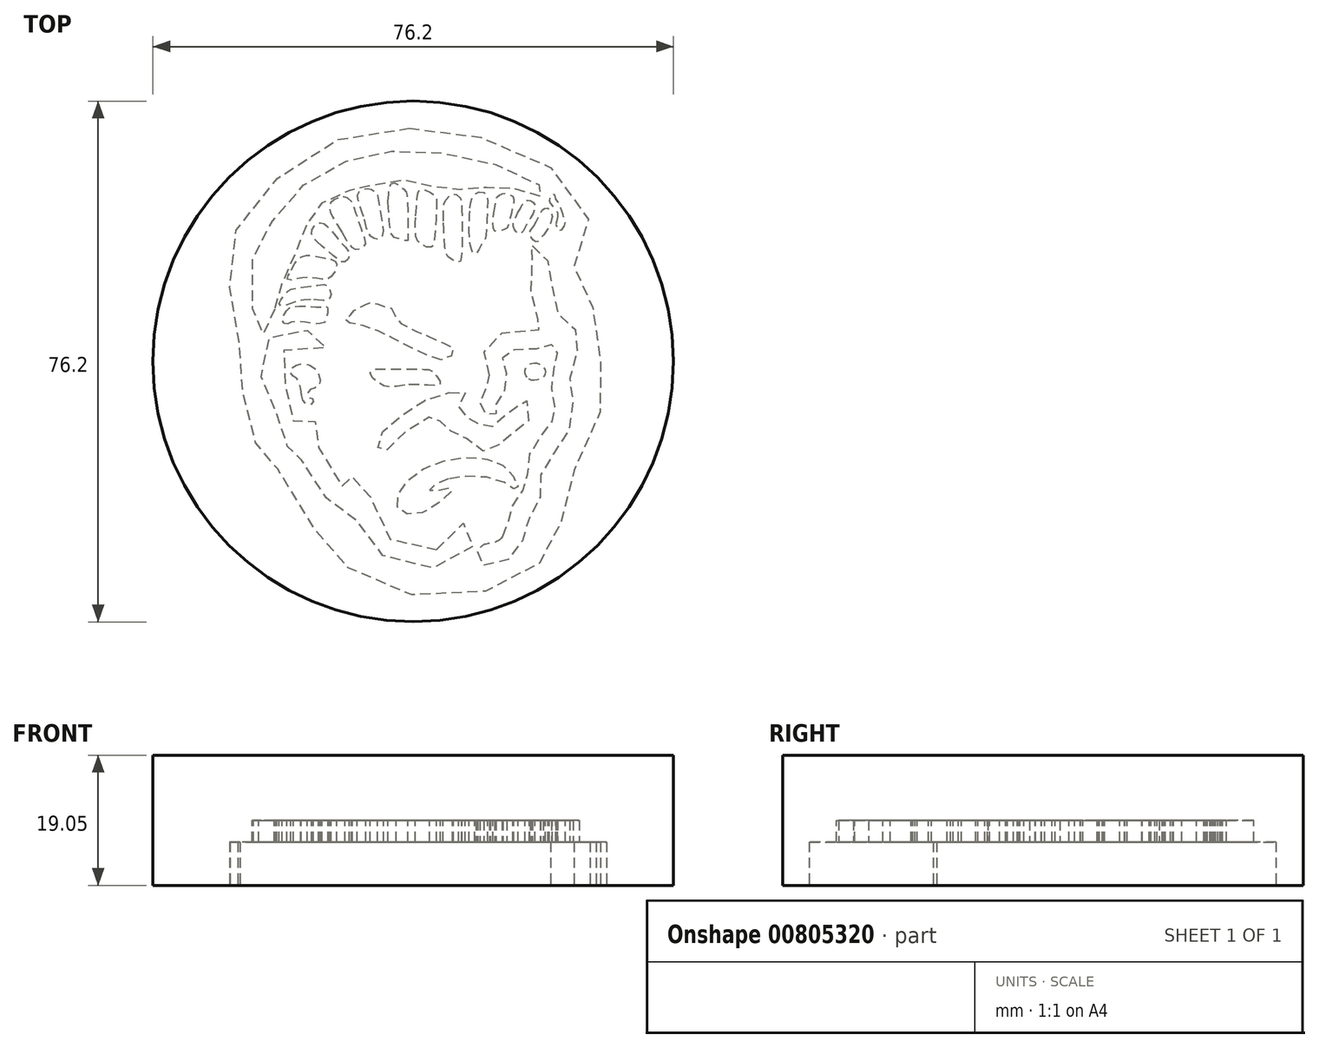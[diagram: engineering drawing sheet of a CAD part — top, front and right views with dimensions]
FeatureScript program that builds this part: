
annotation { "Feature Type Name" : "Feature", "Feature Type Description" : "" }
export const myFeature = defineFeature(function(context is Context, id is Id, definition is map)
    precondition{}
    {
        {
            var Q0;
            Q0=qCreatedBy(makeId("Top.planeOp"),FACE);
            var sketch = newSketch(context, id + "F0", { "sketchPlane" : qUnion([Q0])});
            skCircle(sketch, "E0", {"center": v(-21.46, 11.84) * mm, "radius": 38.1 * mm});
            skFitSpline(sketch, "E1", {"points": [v(-22.7, 8.38) * mm, v(-24.46, 8.12) * mm, v(-25.73, 8.25) * mm, v(-27.12, 9.13) * mm, v(-27.73, 10) * mm, v(-27.64, 10.46) * mm, v(-27.02, 10.74) * mm, v(-25.88, 10.74) * mm, v(-21.93, 10.72) * mm, v(-19.6, 10.7) * mm, v(-19.07, 10.65) * mm, v(-18.56, 10.3) * mm, v(-17.72, 9.25) * mm, v(-17.47, 8.65) * mm, v(-17.68, 8.4) * mm, v(-18.8, 8.34) * mm, v(-21.13, 8.46) * mm, v(-22.7, 8.38) * mm]});
            skFitSpline(sketch, "E2", {"points": [v(-19.46, 15.62) * mm, v(-16.33, 14.26) * mm, v(-15.7, 13.95) * mm, v(-15.58, 13.23) * mm, v(-16.19, 12.4) * mm, v(-17.49, 12.1) * mm, v(-18.69, 12.45) * mm, v(-22.9, 14.45) * mm, v(-26.26, 16.14) * mm, v(-28.77, 17.08) * mm, v(-30.77, 17.49) * mm, v(-31.33, 17.57) * mm, v(-31.4, 17.97) * mm, v(-30.9, 18.38) * mm, v(-30.54, 18.77) * mm, v(-30.4, 19.15) * mm, v(-30.09, 19.33) * mm, v(-29.57, 19.42) * mm, v(-29.27, 19.72) * mm, v(-28.97, 19.97) * mm, v(-28.62, 20.1) * mm, v(-28.14, 20.15) * mm, v(-27.78, 20.44) * mm, v(-27.45, 20.54) * mm, v(-26.96, 20.38) * mm, v(-26.02, 19.96) * mm, v(-25.67, 19.88) * mm, v(-25.26, 19.9) * mm, v(-24.65, 19.6) * mm, v(-24.36, 19.18) * mm, v(-24.08, 18.33) * mm, v(-23.23, 17.37) * mm, v(-20.38, 16) * mm, v(-19.46, 15.62) * mm]});
            skFitSpline(sketch, "E3", {"points": [v(-8.34, -13.71) * mm, v(-9.16, -14.49) * mm, v(-10.62, -14.84) * mm, v(-11.39, -15.13) * mm, v(-12.04, -15.9) * mm], "startDerivative": vector(-2.68, -3.52) * mm, "endDerivative": vector(-2.65, -3.66) * mm});
            skFitSpline(sketch, "E4", {"points": [v(-16.2, 7.28) * mm, v(-14.6, 7.44) * mm, v(-14, 7.47) * mm, v(-13.84, 7.3) * mm, v(-14.14, 6.72) * mm, v(-14.5, 6.33) * mm, v(-14.76, 5.53) * mm, v(-14.79, 4.54) * mm, v(-14.38, 3.83) * mm, v(-13.78, 3.67) * mm, v(-13.2, 3.67) * mm, v(-12.5, 3.43) * mm, v(-12.08, 2.98) * mm, v(-11.38, 2.28) * mm, v(-10.72, 2) * mm, v(-10.17, 2.13) * mm, v(-9.54, 2.62) * mm, v(-8.94, 3.23) * mm, v(-8.52, 3.7) * mm, v(-7.8, 4) * mm, v(-6.7, 4.7) * mm, v(-6.03, 5.35) * mm, v(-5.66, 6.34) * mm, v(-5.45, 6.62) * mm, v(-5.08, 6.51) * mm, v(-4.73, 5.73) * mm, v(-4.46, 4.87) * mm, v(-4.57, 3.19) * mm, v(-5.27, 2.21) * mm, v(-6.6, 1.44) * mm, v(-7.7, 0.95) * mm, v(-8.45, 0.35) * mm, v(-9.08, -0.48) * mm, v(-9.72, -0.93) * mm, v(-10.7, -1.3) * mm, v(-11.63, -1.14) * mm, v(-12.64, -0.36) * mm, v(-13.83, 0.77) * mm, v(-14.43, 1.35) * mm, v(-15.32, 1.58) * mm, v(-16.5, 1.74) * mm, v(-17.1, 2.04) * mm, v(-17.4, 2.69) * mm, v(-17.74, 3.7) * mm, v(-17.86, 3.97) * mm, v(-18.26, 3.98) * mm, v(-19.47, 3.52) * mm, v(-21.5, 2.33) * mm, v(-23.63, 0.73) * mm, v(-25.06, -0.74) * mm, v(-25.75, -1.57) * mm, v(-26.26, -1.64) * mm, v(-26.41, -1.4) * mm, v(-26.65, -0.4) * mm, v(-26.65, 0.63) * mm, v(-26.46, 1.05) * mm, v(-25.12, 2.31) * mm, v(-23.58, 3.62) * mm, v(-21.96, 4.78) * mm, v(-19.93, 6.09) * mm, v(-17.62, 6.91) * mm, v(-16.2, 7.28) * mm]});
            skFitSpline(sketch, "E5", {"points": [v(-10.28, 9.87) * mm, v(-10.8, 11.15) * mm, v(-11.14, 12.51) * mm, v(-10.82, 14.14) * mm, v(-9.8, 15.47) * mm, v(-6.9, 16.25) * mm, v(-3.3, 16.48) * mm, v(-2.63, 16.62) * mm, v(-2.43, 16.79) * mm, v(-2.45, 17.06) * mm, v(-2.8, 17.38) * mm, v(-3.58, 18.79) * mm, v(-4.01, 20.41) * mm, v(-4.22, 23.73) * mm, v(-4.07, 26.05) * mm, v(-4.04, 27.3) * mm, v(-4.26, 28.27) * mm, v(-4.32, 28.66) * mm, v(-4.27, 28.82) * mm, v(-4.11, 28.83) * mm, v(-3.63, 28.66) * mm, v(-2.4, 27.71) * mm, v(-1.66, 26.12) * mm, v(-1.4, 24.83) * mm, v(-1.07, 22.35) * mm, v(-0.84, 20.59) * mm, v(-0.33, 18.92) * mm, v(0.72, 17.53) * mm, v(1.8, 16.95) * mm, v(2.6, 16.11) * mm, v(2.82, 15.4) * mm, v(2.62, 13.6) * mm, v(1.98, 11.41) * mm, v(1.5, 9.72) * mm, v(1.46, 8.37) * mm, v(1.67, 7.02) * mm, v(1.95, 5.46) * mm, v(1.83, 3.42) * mm, v(1.26, 1.69) * mm, v(0.3, 0.12) * mm, v(-0.82, -1.47) * mm, v(-2.19, -3.23) * mm, v(-2.76, -4.53) * mm, v(-2.84, -5.37) * mm, v(-2.78, -6.8) * mm, v(-2.9, -8.04) * mm, v(-3.46, -9.77) * mm, v(-4.42, -11.17) * mm, v(-5.17, -12.34) * mm, v(-5.44, -13.28) * mm, v(-5.5, -14.46) * mm, v(-5.87, -15.61) * mm, v(-7.05, -16.8) * mm, v(-8.61, -17.68) * mm, v(-10.24, -18.06) * mm, v(-11.68, -17.83) * mm, v(-12.24, -17.16) * mm, v(-12.17, -16.33) * mm, v(-12.04, -15.9) * mm], "startDerivative": vector(-31.41, 73.1) * mm, "endDerivative": vector(13.02, 38.55) * mm});
            skFitSpline(sketch, "E6", {"points": [v(-8.34, -13.71) * mm, v(-7.97, -13.17) * mm, v(-7.67, -12.28) * mm, v(-7.45, -10.91) * mm, v(-7.1, -9.74) * mm, v(-6.65, -8.82) * mm, v(-5.7, -7.52) * mm, v(-4.97, -6.2) * mm, v(-4.76, -5.22) * mm, v(-4.62, -3.43) * mm, v(-4.38, -1.8) * mm, v(-3.68, -0.4) * mm, v(-2.64, 1.06) * mm, v(-1.5, 2.47) * mm, v(-0.86, 3.57) * mm, v(-0.62, 4.41) * mm, v(-0.75, 5.56) * mm, v(-1.04, 6.7) * mm, v(-1.2, 8.55) * mm, v(-1.02, 10.18) * mm, v(-0.68, 11.24) * mm, v(-0.4, 12.3) * mm, v(-0.34, 13.63) * mm, v(-0.46, 14.24) * mm, v(-1.03, 14.32) * mm, v(-1.67, 14.21) * mm, v(-2.6, 13.8) * mm, v(-4.73, 13.63) * mm, v(-6.65, 13.56) * mm, v(-7.69, 13.29) * mm, v(-8.34, 12.55) * mm, v(-8.34, 11.43) * mm, v(-7.97, 10.54) * mm, v(-7.79, 9.5) * mm, v(-7.95, 8.16) * mm, v(-8.51, 6.76) * mm, v(-9.16, 6) * mm, v(-9.42, 5.3) * mm, v(-9.51, 4.8) * mm, v(-9.38, 4.46) * mm, v(-9.34, 4.3) * mm, v(-9.44, 3.95) * mm, v(-9.66, 3.78) * mm, v(-10.44, 3.95) * mm, v(-11.25, 4.46) * mm, v(-11.68, 5.16) * mm, v(-11.67, 5.7) * mm, v(-11.14, 7.15) * mm, v(-10.55, 8.4) * mm, v(-10.3, 8.96) * mm, v(-10.2, 9.48) * mm, v(-10.28, 9.87) * mm], "startDerivative": vector(25.13, 32.28) * mm, "endDerivative": vector(-8.83, 30.87) * mm});
            skFitSpline(sketch, "E7", {"points": [v(-16.3, -5.35) * mm, v(-17.56, -5.82) * mm, v(-18.63, -6.38) * mm, v(-19, -6.8) * mm, v(-19.06, -7.06) * mm, v(-18.95, -7.18) * mm, v(-18.44, -7.12) * mm, v(-16.9, -6.78) * mm, v(-15.96, -6.63) * mm, v(-15.75, -6.63) * mm, v(-15.68, -6.77) * mm, v(-15.87, -7.2) * mm, v(-17.23, -8.44) * mm, v(-19.42, -10.03) * mm, v(-21.48, -10.54) * mm, v(-22.84, -10.31) * mm, v(-23.65, -9.65) * mm, v(-23.95, -8.73) * mm, v(-23.49, -7.3) * mm, v(-22.29, -5.6) * mm, v(-19.82, -3.8) * mm, v(-16.58, -2.6) * mm, v(-12.68, -2.18) * mm, v(-9.83, -2.66) * mm, v(-8.1, -3.52) * mm, v(-6.95, -4.79) * mm, v(-6.37, -5.83) * mm, v(-6.14, -6.5) * mm, v(-6.28, -6.87) * mm, v(-6.45, -6.91) * mm, v(-6.72, -6.82) * mm, v(-7.28, -6.32) * mm, v(-8.44, -5.73) * mm, v(-10.94, -5.07) * mm, v(-14.3, -5.02) * mm, v(-16.3, -5.35) * mm]});
            skFitSpline(sketch, "E8", {"points": [v(-37.78, 6.92) * mm, v(-37.98, 8.08) * mm, v(-38.1, 8.82) * mm, v(-38.62, 9.46) * mm, v(-39.1, 9.74) * mm, v(-39.35, 10) * mm, v(-39.35, 10.7) * mm, v(-38.68, 11.25) * mm, v(-37.66, 11.55) * mm, v(-36.18, 11.08) * mm, v(-35.45, 10.27) * mm, v(-35.08, 9.24) * mm, v(-35.25, 8.36) * mm, v(-35.73, 8) * mm, v(-36.32, 7.83) * mm, v(-36.75, 7.55) * mm, v(-36.94, 6.93) * mm, v(-36.58, 6.41) * mm, v(-36.17, 6.4) * mm, v(-36.06, 6.25) * mm, v(-36.2, 5.74) * mm, v(-36.56, 5.5) * mm, v(-37.1, 5.58) * mm, v(-37.58, 6.1) * mm, v(-37.78, 6.92) * mm]});
            skFitSpline(sketch, "E9", {"points": [v(-0.35, 33) * mm, v(-0.52, 32.23) * mm, v(-0.58, 31.86) * mm, v(-0.34, 31.2) * mm, v(0, 30.97) * mm, v(0.3, 31.15) * mm, v(0.74, 31.87) * mm, v(0.8, 32.31) * mm, v(0.58, 32.88) * mm, v(0.37, 33.6) * mm, v(0.15, 34.22) * mm, v(0.08, 34.64) * mm, v(-0.1, 35.06) * mm, v(-0.52, 35.44) * mm, v(-0.73, 36.12) * mm, v(-0.84, 36.3) * mm, v(-1.35, 36.1) * mm, v(-1.5, 35.57) * mm, v(-1.5, 35.14) * mm, v(-1.26, 34.77) * mm, v(-0.64, 34.17) * mm, v(-0.37, 33.68) * mm, v(-0.35, 33) * mm]});
            skFitSpline(sketch, "E10", {"points": [v(-18.03, -15.7) * mm, v(-16.44, -15.2) * mm, v(-15.76, -14.53) * mm, v(-15.18, -13.05) * mm, v(-14.38, -12.02) * mm, v(-13.72, -11.64) * mm, v(-13.19, -11.75) * mm, v(-12.68, -12.16) * mm, v(-12.49, -13.04) * mm, v(-12.48, -14.23) * mm, v(-12.9, -15.59) * mm, v(-13.93, -16.9) * mm, v(-15.22, -17.8) * mm, v(-17.58, -18.33) * mm, v(-20.4, -18.32) * mm, v(-22.73, -17.93) * mm, v(-24.72, -17.19) * mm, v(-26.52, -16.15) * mm, v(-27.86, -14.93) * mm, v(-28.79, -13.4) * mm, v(-29.5, -11.97) * mm, v(-29.65, -11.48) * mm, v(-29.9, -11.26) * mm, v(-31.11, -10.42) * mm, v(-32.43, -9.65) * mm, v(-33.62, -8.69) * mm, v(-35.17, -7.19) * mm, v(-36.5, -5.72) * mm, v(-37.44, -4.06) * mm, v(-37.73, -2.8) * mm, v(-37.94, -1.84) * mm, v(-37.88, -1.01) * mm, v(-37.87, -0.32) * mm, v(-38, -0.14) * mm, v(-39.22, -0.46) * mm, v(-39.8, -0.58) * mm, v(-40.4, -0.48) * mm, v(-40.96, 0.21) * mm, v(-41.15, 1.82) * mm, v(-41.24, 3.22) * mm, v(-41.4, 4.19) * mm, v(-41.43, 5.53) * mm, v(-41.85, 6.91) * mm, v(-42.84, 8.28) * mm, v(-43.7, 9.56) * mm, v(-44.07, 11.28) * mm, v(-43.83, 12.72) * mm, v(-43.23, 14.16) * mm, v(-42.6, 15.23) * mm, v(-42.1, 15.77) * mm, v(-41.78, 15.9) * mm, v(-40.2, 16.08) * mm, v(-37.97, 16.34) * mm, v(-36.78, 16.42) * mm, v(-35.26, 16.4) * mm, v(-34.26, 16.01) * mm, v(-33.91, 15.45) * mm, v(-33.9, 14.62) * mm, v(-34.35, 13.75) * mm, v(-35.4, 13.27) * mm, v(-36.38, 13.16) * mm, v(-37.7, 13.47) * mm, v(-40.42, 13.46) * mm, v(-41.36, 12.87) * mm, v(-41.7, 11.74) * mm, v(-41.37, 10.64) * mm, v(-40.44, 8.94) * mm, v(-39.86, 7.83) * mm, v(-39.45, 6.94) * mm, v(-39.22, 5.52) * mm, v(-39.02, 4) * mm, v(-39.01, 3.04) * mm, v(-39.01, 2.43) * mm, v(-39.01, 2.3) * mm, v(-38.9, 2.28) * mm, v(-37.98, 2.3) * mm, v(-37.15, 2.34) * mm, v(-36.5, 2.67) * mm, v(-35.42, 3.22) * mm, v(-35.06, 3.3) * mm, v(-34.85, 3.19) * mm, v(-34.81, 2.87) * mm, v(-35.03, 1.82) * mm, v(-35.3, -0.2) * mm, v(-35.17, -1.62) * mm, v(-34.56, -3.1) * mm, v(-33.4, -4.75) * mm, v(-32, -6.31) * mm, v(-31.04, -7.24) * mm, v(-30.76, -7.44) * mm, v(-30.44, -7.42) * mm, v(-30.39, -7.16) * mm, v(-30.42, -6.26) * mm, v(-30.47, -5.36) * mm, v(-30.29, -4.8) * mm, v(-29.76, -4.5) * mm, v(-29.06, -4.67) * mm, v(-28.41, -5.14) * mm, v(-28.12, -5.84) * mm, v(-27.56, -8.98) * mm, v(-27.27, -10.6) * mm, v(-26.57, -12.15) * mm, v(-25.24, -13.86) * mm, v(-23.9, -14.7) * mm, v(-21.78, -15.6) * mm, v(-18.95, -15.73) * mm, v(-18.03, -15.7) * mm]});
            skFitSpline(sketch, "E11", {"points": [v(-41.76, 19.52) * mm, v(-41.8, 18.13) * mm, v(-42.27, 16.92) * mm, v(-43.02, 16.42) * mm, v(-43.35, 16.02) * mm, v(-43.41, 15.76) * mm, v(-43.53, 15.67) * mm, v(-43.96, 15.76) * mm, v(-44.4, 16.3) * mm, v(-44.85, 18.35) * mm, v(-45, 20.95) * mm, v(-44.86, 23.72) * mm, v(-44.96, 26.89) * mm, v(-44.78, 28.55) * mm, v(-44.14, 29.62) * mm, v(-42.13, 32.29) * mm, v(-40.8, 34.1) * mm, v(-39.06, 36.15) * mm, v(-36.82, 38.2) * mm, v(-34.37, 39.76) * mm, v(-31.94, 40.88) * mm, v(-29.27, 41.83) * mm, v(-27.07, 42.36) * mm, v(-24.67, 42.6) * mm, v(-22.74, 42.69) * mm, v(-19.66, 42.5) * mm, v(-15.32, 42.13) * mm, v(-11.21, 41.18) * mm, v(-9.13, 40.58) * mm, v(-6.75, 39.58) * mm, v(-4.13, 38.34) * mm, v(-2.5, 37.25) * mm, v(-1.86, 36.63) * mm, v(-1.73, 36.37) * mm, v(-1.95, 36.05) * mm, v(-2.34, 35.65) * mm, v(-2.65, 35.84) * mm, v(-3.12, 36.2) * mm, v(-3.61, 36.48) * mm, v(-4.84, 36.56) * mm, v(-5.74, 36.66) * mm, v(-6.6, 37.08) * mm, v(-7.36, 37.36) * mm, v(-8.7, 37.3) * mm, v(-9.36, 37.05) * mm, v(-10.3, 37.17) * mm, v(-11.06, 37.37) * mm, v(-11.98, 37.37) * mm, v(-12.98, 36.88) * mm, v(-13.62, 36.67) * mm, v(-14.49, 36.96) * mm, v(-15.25, 37.11) * mm, v(-16.31, 37.03) * mm, v(-17.13, 36.8) * mm, v(-18.03, 36.97) * mm, v(-18.96, 37.84) * mm, v(-20.33, 38.14) * mm, v(-21.22, 37.97) * mm, v(-21.98, 38.04) * mm, v(-23.14, 38.52) * mm, v(-24, 38.69) * mm, v(-25.3, 38.54) * mm, v(-25.96, 37.85) * mm, v(-26.72, 37.73) * mm, v(-27.87, 37.77) * mm, v(-29.25, 37.65) * mm, v(-30.12, 37.2) * mm, v(-30.55, 36.9) * mm, v(-31.55, 36.82) * mm, v(-32.56, 36.69) * mm, v(-33.55, 36.2) * mm, v(-34.7, 35.3) * mm, v(-35, 34.39) * mm, v(-35.15, 33.79) * mm, v(-35.7, 33.23) * mm, v(-36.32, 32.9) * mm, v(-37.06, 31.86) * mm, v(-37.54, 30.73) * mm, v(-37.7, 28.97) * mm, v(-37.85, 28.62) * mm, v(-38.16, 28.32) * mm, v(-39.21, 27.19) * mm, v(-40, 26.15) * mm, v(-40.5, 25.05) * mm, v(-40.69, 23.35) * mm, v(-40.76, 22.48) * mm, v(-40.96, 22.22) * mm, v(-41.35, 21.67) * mm, v(-41.72, 20.77) * mm, v(-41.76, 19.52) * mm]});
            skFitSpline(sketch, "E12", {"points": [v(-39.33, 17.58) * mm, v(-39.77, 17.37) * mm, v(-40.12, 17.37) * mm, v(-40.6, 17.63) * mm, v(-40.48, 18.46) * mm, v(-40.05, 19.21) * mm, v(-39.6, 19.66) * mm, v(-38.8, 19.83) * mm, v(-37.6, 19.94) * mm, v(-36.67, 19.88) * mm, v(-35.56, 19.8) * mm, v(-34.7, 19.88) * mm, v(-34.24, 19.96) * mm, v(-33.95, 19.6) * mm, v(-34.07, 18.54) * mm, v(-34.35, 17.65) * mm, v(-34.74, 17.45) * mm, v(-35.64, 17.3) * mm, v(-36.45, 17.45) * mm, v(-37.6, 17.63) * mm, v(-39.33, 17.58) * mm]});
            skFitSpline(sketch, "E13", {"points": [v(-36.44, 20.86) * mm, v(-37.97, 20.81) * mm, v(-39.25, 20.4) * mm, v(-40.42, 19.94) * mm, v(-40.73, 19.9) * mm, v(-41.05, 20.13) * mm, v(-41.03, 20.42) * mm, v(-40.78, 20.95) * mm, v(-40.05, 21.86) * mm, v(-39.64, 22.28) * mm, v(-39.16, 22.44) * mm, v(-37.98, 22.66) * mm, v(-36.5, 22.87) * mm, v(-35.04, 23.05) * mm, v(-34.27, 23.06) * mm, v(-33.89, 22.82) * mm, v(-33.54, 22.03) * mm, v(-33.47, 21.52) * mm, v(-33.72, 21) * mm, v(-34, 20.85) * mm, v(-34.5, 20.75) * mm, v(-35.17, 20.83) * mm, v(-36.44, 20.86) * mm]});
            skFitSpline(sketch, "E14", {"points": [v(-39.31, 25.2) * mm, v(-38.56, 26.57) * mm, v(-38.1, 27) * mm, v(-37.5, 27.3) * mm, v(-36.82, 27.39) * mm, v(-35.87, 27.25) * mm, v(-34.7, 27.01) * mm, v(-33.26, 26.7) * mm, v(-32.8, 26.42) * mm, v(-32.64, 26.1) * mm, v(-32.7, 25.73) * mm, v(-32.93, 24.95) * mm, v(-33.1, 24.69) * mm, v(-33.76, 24.02) * mm, v(-34.41, 23.8) * mm, v(-35.1, 23.93) * mm, v(-36.39, 24.11) * mm, v(-37.98, 24.06) * mm, v(-38.7, 23.86) * mm, v(-39.62, 23.79) * mm, v(-39.92, 23.92) * mm, v(-39.84, 24.22) * mm, v(-39.31, 25.2) * mm]});
            skFitSpline(sketch, "E15", {"points": [v(-34.8, 28.67) * mm, v(-36.21, 30.12) * mm, v(-36.35, 30.7) * mm, v(-36.12, 31.48) * mm, v(-35.46, 32.02) * mm, v(-35, 32.13) * mm, v(-34.35, 31.88) * mm, v(-33.58, 31.09) * mm, v(-32.7, 30.07) * mm, v(-31.63, 28.83) * mm, v(-30.87, 27.73) * mm, v(-30.86, 27.03) * mm, v(-31.4, 26.44) * mm, v(-32, 26.44) * mm, v(-32.88, 27.1) * mm, v(-34.8, 28.67) * mm]});
            skFitSpline(sketch, "E16", {"points": [v(-31.91, 30.73) * mm, v(-31, 29.15) * mm, v(-30.56, 28.65) * mm, v(-30, 28.28) * mm, v(-29.29, 28.3) * mm, v(-28.75, 28.57) * mm, v(-28.41, 29.1) * mm, v(-28.98, 31.09) * mm, v(-29.72, 33.26) * mm, v(-30.34, 35) * mm, v(-30.97, 35.68) * mm, v(-31.66, 35.91) * mm, v(-32.33, 35.77) * mm, v(-33.3, 35.34) * mm, v(-33.67, 34.7) * mm, v(-33.63, 33.9) * mm, v(-33.35, 33.2) * mm, v(-31.91, 30.73) * mm]});
            skFitSpline(sketch, "E17", {"points": [v(-28.67, 32.63) * mm, v(-28.15, 30.8) * mm, v(-27.87, 30.37) * mm, v(-27.06, 29.81) * mm, v(-26.62, 29.77) * mm, v(-26.11, 29.95) * mm, v(-25.9, 30.35) * mm, v(-25.82, 31.26) * mm, v(-26.23, 33.91) * mm, v(-26.55, 35.82) * mm, v(-26.82, 36.42) * mm, v(-27.49, 36.9) * mm, v(-28.23, 37.07) * mm, v(-29.1, 36.85) * mm, v(-29.58, 36.4) * mm, v(-29.64, 35.85) * mm, v(-29.38, 34.9) * mm, v(-28.67, 32.63) * mm]});
            skFitSpline(sketch, "E18", {"points": [v(-25.14, 35.22) * mm, v(-24.93, 37.26) * mm, v(-24.73, 37.82) * mm, v(-24.3, 37.97) * mm, v(-23.7, 37.72) * mm, v(-22.67, 36.87) * mm, v(-22.44, 36.5) * mm, v(-22.33, 36) * mm, v(-22.24, 33.1) * mm, v(-22.21, 30.55) * mm, v(-22.22, 29.61) * mm, v(-22.28, 29.46) * mm, v(-22.83, 29.57) * mm, v(-24.15, 29.97) * mm, v(-24.66, 30.54) * mm, v(-24.92, 32.1) * mm, v(-25.06, 34.07) * mm, v(-25.14, 35.22) * mm]});
            skFitSpline(sketch, "E19", {"points": [v(-21.08, 33.16) * mm, v(-20.87, 35.88) * mm, v(-20.72, 36.67) * mm, v(-20.41, 37) * mm, v(-19.98, 37.03) * mm, v(-19.36, 36.79) * mm, v(-18.35, 36.15) * mm, v(-18.07, 35.64) * mm, v(-18.02, 34.9) * mm, v(-18.18, 32.04) * mm, v(-18.51, 28.8) * mm, v(-18.63, 28.65) * mm, v(-19.18, 28.5) * mm, v(-20.17, 28.92) * mm, v(-20.9, 29.6) * mm, v(-21.14, 31.32) * mm, v(-21.08, 33.16) * mm]});
            skFitSpline(sketch, "E20", {"points": [v(-17.06, 32.41) * mm, v(-16.97, 34.72) * mm, v(-16.8, 35.25) * mm, v(-16.35, 35.9) * mm, v(-15.62, 36.3) * mm, v(-15.37, 36.34) * mm, v(-15.08, 36.24) * mm, v(-14.52, 35.71) * mm, v(-14.34, 34.83) * mm, v(-14.33, 32.77) * mm, v(-14.28, 30.12) * mm, v(-14.4, 27.24) * mm, v(-14.5, 26.6) * mm, v(-14.83, 26.3) * mm, v(-15.26, 26.47) * mm, v(-16.23, 27.01) * mm, v(-16.59, 27.44) * mm, v(-16.78, 28.15) * mm, v(-16.94, 30.31) * mm, v(-17.06, 32.41) * mm]});
            skFitSpline(sketch, "E21", {"points": [v(-13.15, 34.3) * mm, v(-13.01, 35.32) * mm, v(-12.72, 36) * mm, v(-12.1, 36.5) * mm, v(-11.6, 36.63) * mm, v(-10.83, 36.45) * mm, v(-10.6, 35.97) * mm, v(-10.62, 33.4) * mm, v(-10.74, 31.17) * mm, v(-10.9, 29.84) * mm, v(-10.98, 29.66) * mm, v(-11.55, 28.87) * mm, v(-12.2, 27.66) * mm, v(-12.36, 27.63) * mm, v(-12.73, 27.64) * mm, v(-12.82, 27.84) * mm, v(-13.09, 28.77) * mm, v(-13.26, 30.35) * mm, v(-13.25, 32.55) * mm, v(-13.15, 34.3) * mm]});
            skFitSpline(sketch, "E22", {"points": [v(-9.64, 33.51) * mm, v(-9.3, 35.68) * mm, v(-9.22, 35.89) * mm, v(-8.65, 36.3) * mm, v(-8.2, 36.42) * mm, v(-7.76, 36.4) * mm, v(-6.9, 35.99) * mm, v(-6.72, 35.56) * mm, v(-6.81, 34.83) * mm, v(-7.15, 33.37) * mm, v(-7.61, 31.53) * mm, v(-7.73, 31.37) * mm, v(-8.16, 31.1) * mm, v(-9.03, 30.84) * mm, v(-9.4, 30.86) * mm, v(-9.68, 31.08) * mm, v(-9.79, 32.51) * mm, v(-9.64, 33.51) * mm]});
            skFitSpline(sketch, "E23", {"points": [v(-6.15, 33.57) * mm, v(-5.46, 34.84) * mm, v(-5.23, 35.23) * mm, v(-4.75, 35.4) * mm, v(-4.12, 35.27) * mm, v(-3.63, 34.71) * mm, v(-3.92, 33.46) * mm, v(-5, 31.62) * mm, v(-5.64, 30.6) * mm, v(-6.2, 30.61) * mm, v(-6.7, 31.27) * mm, v(-6.85, 31.72) * mm, v(-6.72, 32.36) * mm, v(-6.15, 33.57) * mm]});
            skFitSpline(sketch, "E24", {"points": [v(-3.85, 31.62) * mm, v(-2.92, 33.33) * mm, v(-2.59, 33.99) * mm, v(-2.31, 34.21) * mm, v(-1.74, 34.26) * mm, v(-1.43, 34) * mm, v(-1.1, 33.14) * mm, v(-1.2, 32.62) * mm, v(-1.54, 31.63) * mm, v(-2.26, 30.5) * mm, v(-3.1, 29.48) * mm, v(-3.42, 29.3) * mm, v(-3.8, 29.5) * mm, v(-4.34, 30.22) * mm, v(-4.46, 30.56) * mm, v(-4.33, 30.87) * mm, v(-3.85, 31.62) * mm]});
            skFitSpline(sketch, "E25", {"points": [v(-4.77, 9.5) * mm, v(-5.07, 10.15) * mm, v(-4.95, 10.97) * mm, v(-4.45, 11.45) * mm, v(-3.72, 11.63) * mm, v(-2.73, 11.33) * mm, v(-2.25, 10.78) * mm, v(-2.1, 10.18) * mm, v(-2.46, 9.5) * mm, v(-3.2, 9.15) * mm, v(-4.13, 9.1) * mm, v(-4.77, 9.5) * mm]});
            skFitSpline(sketch, "E26", {"points": [v(-22.05, 45.95) * mm, v(-17.92, 45.68) * mm, v(-11.6, 44.65) * mm, v(-5.61, 42.66) * mm, v(-0.67, 39.74) * mm, v(3.08, 35.89) * mm, v(4.17, 32.77) * mm, v(4.3, 30.75) * mm, v(2.35, 27.01) * mm, v(2.08, 25.88) * mm, v(2.6, 22.98) * mm, v(3.24, 20.67) * mm, v(4.62, 19.86) * mm, v(6.24, 18.53) * mm, v(6.8, 15.12) * mm, v(5.46, 9.9) * mm, v(5.43, 7.3) * mm, v(5.73, 5.27) * mm, v(5.83, 2.93) * mm, v(3.06, -2.52) * mm, v(1.93, -4.48) * mm, v(1.7, -6.5) * mm, v(1.22, -9.78) * mm, v(-1.03, -13.64) * mm, v(-1.33, -14.77) * mm, v(-1.45, -15.8) * mm, v(-3.92, -18.48) * mm, v(-6.88, -20.35) * mm, v(-10.55, -21.71) * mm, v(-14.6, -22.17) * mm, v(-21.46, -22.33) * mm, v(-26.7, -21.2) * mm, v(-30.8, -18.56) * mm, v(-32.67, -15.5) * mm, v(-33.62, -14.15) * mm, v(-36.3, -12.46) * mm, v(-40.46, -7.66) * mm, v(-41.37, -3.76) * mm, v(-41.64, -3.78) * mm, v(-42.88, -4.22) * mm, v(-43.82, -3.24) * mm, v(-44.64, 1.28) * mm, v(-44.86, 4.54) * mm, v(-45.84, 6.58) * mm, v(-47, 8.65) * mm, v(-47, 11.84) * mm, v(-46.88, 14.32) * mm, v(-47.44, 16.22) * mm, v(-48.28, 19.88) * mm, v(-48.3, 23.58) * mm, v(-48.28, 28.76) * mm, v(-48.22, 29) * mm, v(-47.18, 31.44) * mm, v(-44.86, 34.56) * mm, v(-41.6, 38.38) * mm, v(-37.42, 41.78) * mm, v(-32.72, 44.22) * mm, v(-28.04, 45.58) * mm, v(-22.05, 45.95) * mm]});
            skSolve(sketch);
        }
        {
            var Q0;
            Q0=makeQuery(id+"F0.imprint","IMPRINT",FACE,{"disambiguationData":[TD([[makeQuery(id+"F0.imprint","IMPRINT",EDGE,{"derivedFrom":sQuery(id+"F0.wireOp",EDGE,"E0")}),1.0]])]});
            var Q1;
            Q1=makeQuery(id+"F0.imprint","IMPRINT",FACE,{"disambiguationData":[TD([[makeQuery(id+"F0.imprint","IMPRINT",EDGE,{"derivedFrom":sQuery(id+"F0.wireOp",EDGE,"E1")}),1.0]])]});
            var Q2;
            Q2=makeQuery(id+"F0.imprint","IMPRINT",FACE,{"disambiguationData":[TD([[makeQuery(id+"F0.imprint","IMPRINT",EDGE,{"derivedFrom":sQuery(id+"F0.wireOp",EDGE,"E3")}),1.0]])]});
            var Q3;
            Q3=makeQuery(id+"F0.imprint","IMPRINT",FACE,{"disambiguationData":[TD([[makeQuery(id+"F0.imprint","IMPRINT",EDGE,{"derivedFrom":sQuery(id+"F0.wireOp",EDGE,"E4")}),-1.0]])]});
            var Q4;
            Q4=makeQuery(id+"F0.imprint","IMPRINT",FACE,{"disambiguationData":[TD([[makeQuery(id+"F0.imprint","IMPRINT",EDGE,{"derivedFrom":sQuery(id+"F0.wireOp",EDGE,"E7")}),-1.0]])]});
            var Q5;
            Q5=makeQuery(id+"F0.imprint","IMPRINT",FACE,{"disambiguationData":[TD([[makeQuery(id+"F0.imprint","IMPRINT",EDGE,{"derivedFrom":sQuery(id+"F0.wireOp",EDGE,"E10")}),-1.0]])]});
            var Q6;
            Q6=makeQuery(id+"F0.imprint","IMPRINT",FACE,{"disambiguationData":[TD([[makeQuery(id+"F0.imprint","IMPRINT",EDGE,{"derivedFrom":sQuery(id+"F0.wireOp",EDGE,"E12")}),-1.0]])]});
            var Q7;
            Q7=makeQuery(id+"F0.imprint","IMPRINT",FACE,{"disambiguationData":[TD([[makeQuery(id+"F0.imprint","IMPRINT",EDGE,{"derivedFrom":sQuery(id+"F0.wireOp",EDGE,"E8")}),-1.0]])]});
            var Q8;
            Q8=makeQuery(id+"F0.imprint","IMPRINT",FACE,{"disambiguationData":[TD([[makeQuery(id+"F0.imprint","IMPRINT",EDGE,{"derivedFrom":sQuery(id+"F0.wireOp",EDGE,"E1")}),-1.0]])]});
            var Q9;
            Q9=makeQuery(id+"F0.imprint","IMPRINT",FACE,{"disambiguationData":[TD([[makeQuery(id+"F0.imprint","IMPRINT",EDGE,{"derivedFrom":sQuery(id+"F0.wireOp",EDGE,"E2")}),-1.0]])]});
            var Q10;
            Q10=makeQuery(id+"F0.imprint","IMPRINT",FACE,{"disambiguationData":[TD([[makeQuery(id+"F0.imprint","IMPRINT",EDGE,{"derivedFrom":sQuery(id+"F0.wireOp",EDGE,"E25")}),-1.0]])]});
            var Q11;
            Q11=makeQuery(id+"F0.imprint","IMPRINT",FACE,{"disambiguationData":[TD([[makeQuery(id+"F0.imprint","IMPRINT",EDGE,{"derivedFrom":sQuery(id+"F0.wireOp",EDGE,"E16")}),1.0]])]});
            var Q12;
            Q12=makeQuery(id+"F0.imprint","IMPRINT",FACE,{"disambiguationData":[TD([[makeQuery(id+"F0.imprint","IMPRINT",EDGE,{"derivedFrom":sQuery(id+"F0.wireOp",EDGE,"E15")}),-1.0]])]});
            var Q13;
            Q13=makeQuery(id+"F0.imprint","IMPRINT",FACE,{"disambiguationData":[TD([[makeQuery(id+"F0.imprint","IMPRINT",EDGE,{"derivedFrom":sQuery(id+"F0.wireOp",EDGE,"E14")}),-1.0]])]});
            var Q14;
            Q14=makeQuery(id+"F0.imprint","IMPRINT",FACE,{"disambiguationData":[TD([[makeQuery(id+"F0.imprint","IMPRINT",EDGE,{"derivedFrom":sQuery(id+"F0.wireOp",EDGE,"E13")}),-1.0]])]});
            var Q15;
            Q15=makeQuery(id+"F0.imprint","IMPRINT",FACE,{"disambiguationData":[TD([[makeQuery(id+"F0.imprint","IMPRINT",EDGE,{"derivedFrom":sQuery(id+"F0.wireOp",EDGE,"E11")}),-1.0]])]});
            var Q16;
            Q16=makeQuery(id+"F0.imprint","IMPRINT",FACE,{"disambiguationData":[TD([[makeQuery(id+"F0.imprint","IMPRINT",EDGE,{"derivedFrom":sQuery(id+"F0.wireOp",EDGE,"E17")}),1.0]])]});
            var Q17;
            Q17=makeQuery(id+"F0.imprint","IMPRINT",FACE,{"disambiguationData":[TD([[makeQuery(id+"F0.imprint","IMPRINT",EDGE,{"derivedFrom":sQuery(id+"F0.wireOp",EDGE,"E18")}),-1.0]])]});
            var Q18;
            Q18=makeQuery(id+"F0.imprint","IMPRINT",FACE,{"disambiguationData":[TD([[makeQuery(id+"F0.imprint","IMPRINT",EDGE,{"derivedFrom":sQuery(id+"F0.wireOp",EDGE,"E19")}),-1.0]])]});
            var Q19;
            Q19=makeQuery(id+"F0.imprint","IMPRINT",FACE,{"disambiguationData":[TD([[makeQuery(id+"F0.imprint","IMPRINT",EDGE,{"derivedFrom":sQuery(id+"F0.wireOp",EDGE,"E20")}),-1.0]])]});
            var Q20;
            Q20=makeQuery(id+"F0.imprint","IMPRINT",FACE,{"disambiguationData":[TD([[makeQuery(id+"F0.imprint","IMPRINT",EDGE,{"derivedFrom":sQuery(id+"F0.wireOp",EDGE,"E21")}),-1.0]])]});
            var Q21;
            Q21=makeQuery(id+"F0.imprint","IMPRINT",FACE,{"disambiguationData":[TD([[makeQuery(id+"F0.imprint","IMPRINT",EDGE,{"derivedFrom":sQuery(id+"F0.wireOp",EDGE,"E22")}),-1.0]])]});
            var Q22;
            Q22=makeQuery(id+"F0.imprint","IMPRINT",FACE,{"disambiguationData":[TD([[makeQuery(id+"F0.imprint","IMPRINT",EDGE,{"derivedFrom":sQuery(id+"F0.wireOp",EDGE,"E23")}),-1.0]])]});
            var Q23;
            Q23=makeQuery(id+"F0.imprint","IMPRINT",FACE,{"disambiguationData":[TD([[makeQuery(id+"F0.imprint","IMPRINT",EDGE,{"derivedFrom":sQuery(id+"F0.wireOp",EDGE,"E24")}),-1.0]])]});
            var Q24;
            Q24=makeQuery(id+"F0.imprint","IMPRINT",FACE,{"disambiguationData":[TD([[makeQuery(id+"F0.imprint","IMPRINT",EDGE,{"derivedFrom":sQuery(id+"F0.wireOp",EDGE,"E9")}),1.0]])]});
            extrude(context, id + "F1", {"entities" : qUnion([Q0, Q1, Q2, Q3, Q4, Q5, Q6, Q7, Q8, Q9, Q10, Q11, Q12, Q13, Q14, Q15, Q16, Q17, Q18, Q19, Q20, Q21, Q22, Q23, Q24]), "depth" : 19.05 * mm, "offsetDistance" : 25.4 * mm});
        }
        {
            var Q0;
            Q0=makeQuery(id+"F0.imprint","IMPRINT",FACE,{"disambiguationData":[TD([[makeQuery(id+"F0.imprint","IMPRINT",EDGE,{"derivedFrom":sQuery(id+"F0.wireOp",EDGE,"E10")}),-1.0]])]});
            var Q1;
            Q1=makeQuery(id+"F0.imprint","IMPRINT",FACE,{"disambiguationData":[TD([[makeQuery(id+"F0.imprint","IMPRINT",EDGE,{"derivedFrom":sQuery(id+"F0.wireOp",EDGE,"E11")}),-1.0]])]});
            var Q2;
            Q2=makeQuery(id+"F0.imprint","IMPRINT",FACE,{"disambiguationData":[TD([[makeQuery(id+"F0.imprint","IMPRINT",EDGE,{"derivedFrom":sQuery(id+"F0.wireOp",EDGE,"E12")}),-1.0]])]});
            var Q3;
            Q3=makeQuery(id+"F0.imprint","IMPRINT",FACE,{"disambiguationData":[TD([[makeQuery(id+"F0.imprint","IMPRINT",EDGE,{"derivedFrom":sQuery(id+"F0.wireOp",EDGE,"E13")}),-1.0]])]});
            var Q4;
            Q4=makeQuery(id+"F0.imprint","IMPRINT",FACE,{"disambiguationData":[TD([[makeQuery(id+"F0.imprint","IMPRINT",EDGE,{"derivedFrom":sQuery(id+"F0.wireOp",EDGE,"E14")}),-1.0]])]});
            var Q5;
            Q5=makeQuery(id+"F0.imprint","IMPRINT",FACE,{"disambiguationData":[TD([[makeQuery(id+"F0.imprint","IMPRINT",EDGE,{"derivedFrom":sQuery(id+"F0.wireOp",EDGE,"E15")}),-1.0]])]});
            var Q6;
            Q6=makeQuery(id+"F0.imprint","IMPRINT",FACE,{"disambiguationData":[TD([[makeQuery(id+"F0.imprint","IMPRINT",EDGE,{"derivedFrom":sQuery(id+"F0.wireOp",EDGE,"E16")}),1.0]])]});
            var Q7;
            Q7=makeQuery(id+"F0.imprint","IMPRINT",FACE,{"disambiguationData":[TD([[makeQuery(id+"F0.imprint","IMPRINT",EDGE,{"derivedFrom":sQuery(id+"F0.wireOp",EDGE,"E17")}),1.0]])]});
            var Q8;
            Q8=makeQuery(id+"F0.imprint","IMPRINT",FACE,{"disambiguationData":[TD([[makeQuery(id+"F0.imprint","IMPRINT",EDGE,{"derivedFrom":sQuery(id+"F0.wireOp",EDGE,"E18")}),-1.0]])]});
            var Q9;
            Q9=makeQuery(id+"F0.imprint","IMPRINT",FACE,{"disambiguationData":[TD([[makeQuery(id+"F0.imprint","IMPRINT",EDGE,{"derivedFrom":sQuery(id+"F0.wireOp",EDGE,"E19")}),-1.0]])]});
            var Q10;
            Q10=makeQuery(id+"F0.imprint","IMPRINT",FACE,{"disambiguationData":[TD([[makeQuery(id+"F0.imprint","IMPRINT",EDGE,{"derivedFrom":sQuery(id+"F0.wireOp",EDGE,"E20")}),-1.0]])]});
            var Q11;
            Q11=makeQuery(id+"F0.imprint","IMPRINT",FACE,{"disambiguationData":[TD([[makeQuery(id+"F0.imprint","IMPRINT",EDGE,{"derivedFrom":sQuery(id+"F0.wireOp",EDGE,"E21")}),-1.0]])]});
            var Q12;
            Q12=makeQuery(id+"F0.imprint","IMPRINT",FACE,{"disambiguationData":[TD([[makeQuery(id+"F0.imprint","IMPRINT",EDGE,{"derivedFrom":sQuery(id+"F0.wireOp",EDGE,"E22")}),-1.0]])]});
            var Q13;
            Q13=makeQuery(id+"F0.imprint","IMPRINT",FACE,{"disambiguationData":[TD([[makeQuery(id+"F0.imprint","IMPRINT",EDGE,{"derivedFrom":sQuery(id+"F0.wireOp",EDGE,"E23")}),-1.0]])]});
            var Q14;
            Q14=makeQuery(id+"F0.imprint","IMPRINT",FACE,{"disambiguationData":[TD([[makeQuery(id+"F0.imprint","IMPRINT",EDGE,{"derivedFrom":sQuery(id+"F0.wireOp",EDGE,"E24")}),-1.0]])]});
            var Q15;
            Q15=makeQuery(id+"F0.imprint","IMPRINT",FACE,{"disambiguationData":[TD([[makeQuery(id+"F0.imprint","IMPRINT",EDGE,{"derivedFrom":sQuery(id+"F0.wireOp",EDGE,"E9")}),1.0]])]});
            var Q16;
            Q16=makeQuery(id+"F0.imprint","IMPRINT",FACE,{"disambiguationData":[TD([[makeQuery(id+"F0.imprint","IMPRINT",EDGE,{"derivedFrom":sQuery(id+"F0.wireOp",EDGE,"E3")}),1.0]])]});
            var Q17;
            Q17=makeQuery(id+"F0.imprint","IMPRINT",FACE,{"disambiguationData":[TD([[makeQuery(id+"F0.imprint","IMPRINT",EDGE,{"derivedFrom":sQuery(id+"F0.wireOp",EDGE,"E2")}),-1.0]])]});
            var Q18;
            Q18=makeQuery(id+"F0.imprint","IMPRINT",FACE,{"disambiguationData":[TD([[makeQuery(id+"F0.imprint","IMPRINT",EDGE,{"derivedFrom":sQuery(id+"F0.wireOp",EDGE,"E1")}),-1.0]])]});
            var Q19;
            Q19=makeQuery(id+"F0.imprint","IMPRINT",FACE,{"disambiguationData":[TD([[makeQuery(id+"F0.imprint","IMPRINT",EDGE,{"derivedFrom":sQuery(id+"F0.wireOp",EDGE,"E8")}),-1.0]])]});
            var Q20;
            Q20=makeQuery(id+"F0.imprint","IMPRINT",FACE,{"disambiguationData":[TD([[makeQuery(id+"F0.imprint","IMPRINT",EDGE,{"derivedFrom":sQuery(id+"F0.wireOp",EDGE,"E4")}),-1.0]])]});
            var Q21;
            Q21=makeQuery(id+"F0.imprint","IMPRINT",FACE,{"disambiguationData":[TD([[makeQuery(id+"F0.imprint","IMPRINT",EDGE,{"derivedFrom":sQuery(id+"F0.wireOp",EDGE,"E25")}),-1.0]])]});
            var Q22;
            Q22=makeQuery(id+"F0.imprint","IMPRINT",FACE,{"disambiguationData":[TD([[makeQuery(id+"F0.imprint","IMPRINT",EDGE,{"derivedFrom":sQuery(id+"F0.wireOp",EDGE,"E7")}),-1.0]])]});
            extrude(context, id + "F2", {"entities" : qUnion([Q0, Q1, Q2, Q3, Q4, Q5, Q6, Q7, Q8, Q9, Q10, Q11, Q12, Q13, Q14, Q15, Q16, Q17, Q18, Q19, Q20, Q21, Q22]), "operationType" : NewBodyOperationType.REMOVE, "depth" : 9.52 * mm, "offsetDistance" : 25.4 * mm});
        }
        {
            var Q0;
            Q0=makeQuery(id+"F0.imprint","IMPRINT",FACE,{"disambiguationData":[TD([[makeQuery(id+"F0.imprint","IMPRINT",EDGE,{"derivedFrom":sQuery(id+"F0.wireOp",EDGE,"E1")}),1.0]])]});
            extrude(context, id + "F3", {"entities" : qUnion([Q0]), "operationType" : NewBodyOperationType.REMOVE, "depth" : 6.35 * mm, "offsetDistance" : 25.4 * mm});
        }
    });
